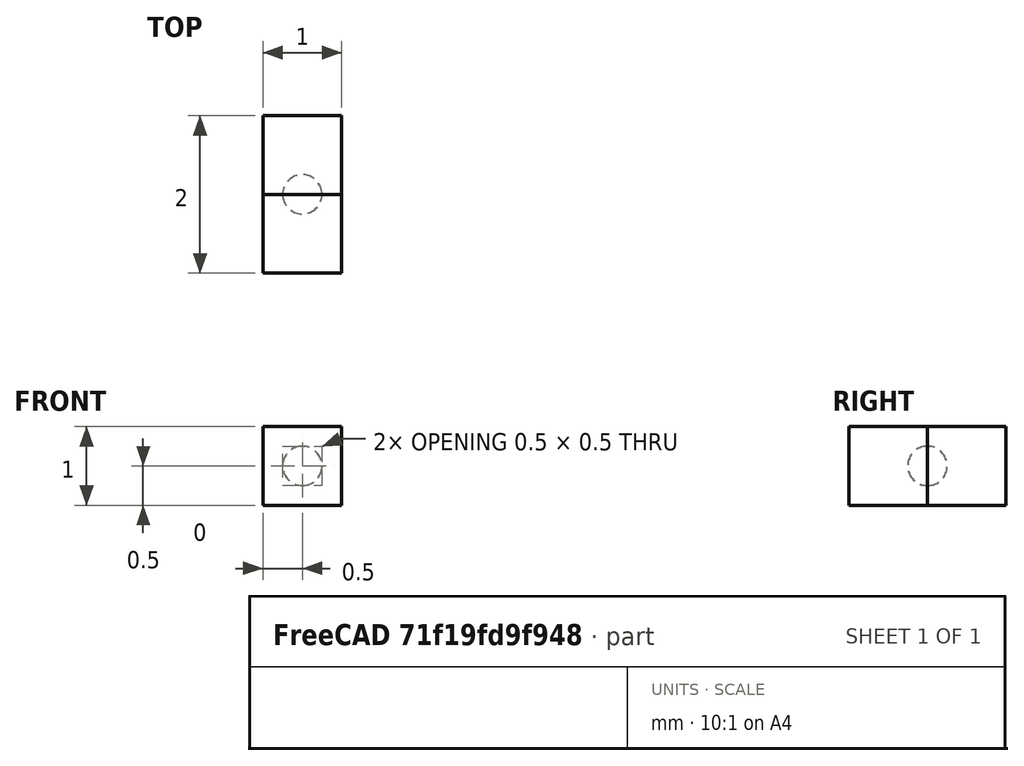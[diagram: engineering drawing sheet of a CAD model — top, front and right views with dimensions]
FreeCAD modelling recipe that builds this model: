
FCSTD DOCUMENT  (FreeCAD 0.22R37442 (Git))
Label: sphere-immersed-in-two-boxes
License: All rights reserved
LicenseURL: https://en.wikipedia.org/wiki/All_rights_reserved
objects: Part::Sphere×3, Part::Box×2, Part::Cut×2, Part::Feature×2, Part::FeaturePython×2
note: 11 computed .brp shape members not serialized (recipe doc carries the construction recipe); baked Part::Feature solids carry a one-line shape summary decoded from their .brp

FEATURE [Part::Box] Box  label="Cube"
  AttacherType = Attacher::AttachEngine3D
  Height = 1
  Length = 1
  Placement = pos=(-0.5,-1,-0.5) rot=(0,0,1;0rad)
  Width = 1
FEATURE [Part::Box] Box001  label="Cube001"
  AttacherType = Attacher::AttachEngine3D
  Height = 1
  Length = 1
  Placement = pos=(-0.5,0,-0.5) rot=(0,0,1;0rad)
  Width = 1
FEATURE [Part::Sphere] Sphere
  Angle1 = -90
  Angle2 = 90
  Angle3 = 360
  AttacherType = Attacher::AttachEngine3D
  Radius = 0.25
FEATURE [Part::Sphere] Sphere001
  Angle1 = -90
  Angle2 = 90
  Angle3 = 360
  AttacherType = Attacher::AttachEngine3D
  Radius = 0.25
FEATURE [Part::Cut] Cut
  Base = -> Box
  Tool = -> Sphere
FEATURE [Part::Sphere] Sphere002
  Angle1 = -90
  Angle2 = 90
  Angle3 = 360
  AttacherType = Attacher::AttachEngine3D
  Radius = 0.25
FEATURE [Part::Cut] Cut001
  Base = -> Box001
  Tool = -> Sphere001
FEATURE [Part::Feature] Cut_solid  label="Cut (Solid)"
  shape: bbox 1 x 1 x 1 mm, 7 faces (baked)
FEATURE [Part::Feature] Cut001_solid  label="Cut001 (Solid)"
  shape: bbox 1 x 1 x 1 mm, 7 faces (baked)
FEATURE [Part::FeaturePython] BooleanFragments  # WARN: FeaturePython — macro-defined, semantics opaque (R4)
  Mode = 2
  Objects = -> [Sphere002,Cut_solid,Cut001_solid]
  Tolerance = 0
FEATURE [Part::FeaturePython] CompoundFilter  # WARN: FeaturePython — macro-defined, semantics opaque (R4)
  Base = -> BooleanFragments
  FilterType = 3
  Invert = false
  OverrideMaxVal = 0
  WindowFrom = 80
  WindowTo = 100
